# Revit family: Gira_510300
name_source: partatom
category: Generic Models
revit_build: Autodesk Revit 2017 (Build: 20160225_1515(x64)
units: mm (PartAtom-declared; Revit-internal decimal feet)

## family parameters
Can host rebar = No
Cut with Voids When Loaded = No
Host = Face
Part Type = Normal
Room Calculation Point = No
Round Connector Dimension = Use Diameter
Shared = No

## types (1)
- RF PB sens. 3-g KNX
    BIM = https://media.live.bim.site
    BIMSITE_PRODUCT_ID = c2e1978726a777219db44485629d34b0aefbabc7
    Bus connection included = No
    Colour = Sonstige (*de-DE)
    Cost = 0 $
    Default Elevation = 1219 mm
    Description = RF PB sens.3g KNX KNX RF pushbutton sensor 3-gang System 55   Gira E22 Start-up rocker The KNX RF pushbutton sensors transmit KNX telegrams wirelessly when the button is pressed, depending on the parameter settings when the application program is loaded. These could be e.g. telegrams for switching pressing, for dimming or blind control. It is also possible to program encoder functions (dimming encoders and scene auxiliary units).,Features: - Confirmation function as well as transmit and status display via two-colour LED (red green) separately for each button by 2-stage display function. - Optional status display by separate 1-bit status communication objects. - Transmit and confirmation display deactivatable. - The pushbutton sensor can be attached to walls using screws or affixed to smooth or transparent surfaces using a mounting plate. - Project planning, start-up and parameter setting are performed using ETS (version 5 or later). - Battery-operated device. Switching" function: - Rocker or button function. - Command for pressing and releasing can be parameterised (ON, OFF, CHANGE, no reaction). "Dimming" function: - Rocker function. - Command when the rocker is pressed (right and left button) can be set in the parameters (lighter - ON, darker - OFF). "Blind" function: - Rocker function. - Command when the rocker is pressed (right and left button) can be set in the parameters (ON, OFF, CHANGE). - Time between short and long-term command can be set in the parameters. "Value transmitter" and "Scene auxiliary unit" functions: - Rocker function. - Command when the rocker is pressed (right and left button) can be set in the parameters (values 0 to 255, 0 to 100% or scene number). - With scene auxiliary unit: Memory function possible.,Notes : - Batteries are consumables and must be replaced regularly. Please observe the regulations on the disposal of used batteries. - The pushbutton sensor is supplied with a program-neutral start-up rocker. The suitable rocker set for the design line must be ordered separately. - The range can be reduced when using rocker sets and or cover frames."
    GTIN = 4010337017257
    HAN = 510300
    HeinzeBIM = https://www.heinze.de
    Manufacturer = Gira
    Material = Sonstige (*de-DE)
    Material quality = Sonstige (*de-DE)
    Number of actuation points = 6
    Number of buttons = 3
    Surface finishing = Not applicable
    Surface protection = Sonstige (*de-DE)
    Transparent = No
    URL = https://www.gira.de
    With IR sensor = No
    With anti-theft/dismantling protection = No
    With display = No
    With label area = No
    With room temperature controller = No

## geometry (parser evidence)
native form markers: Blend x2, Sweep x3
no freeform markers — native parametric forms only
